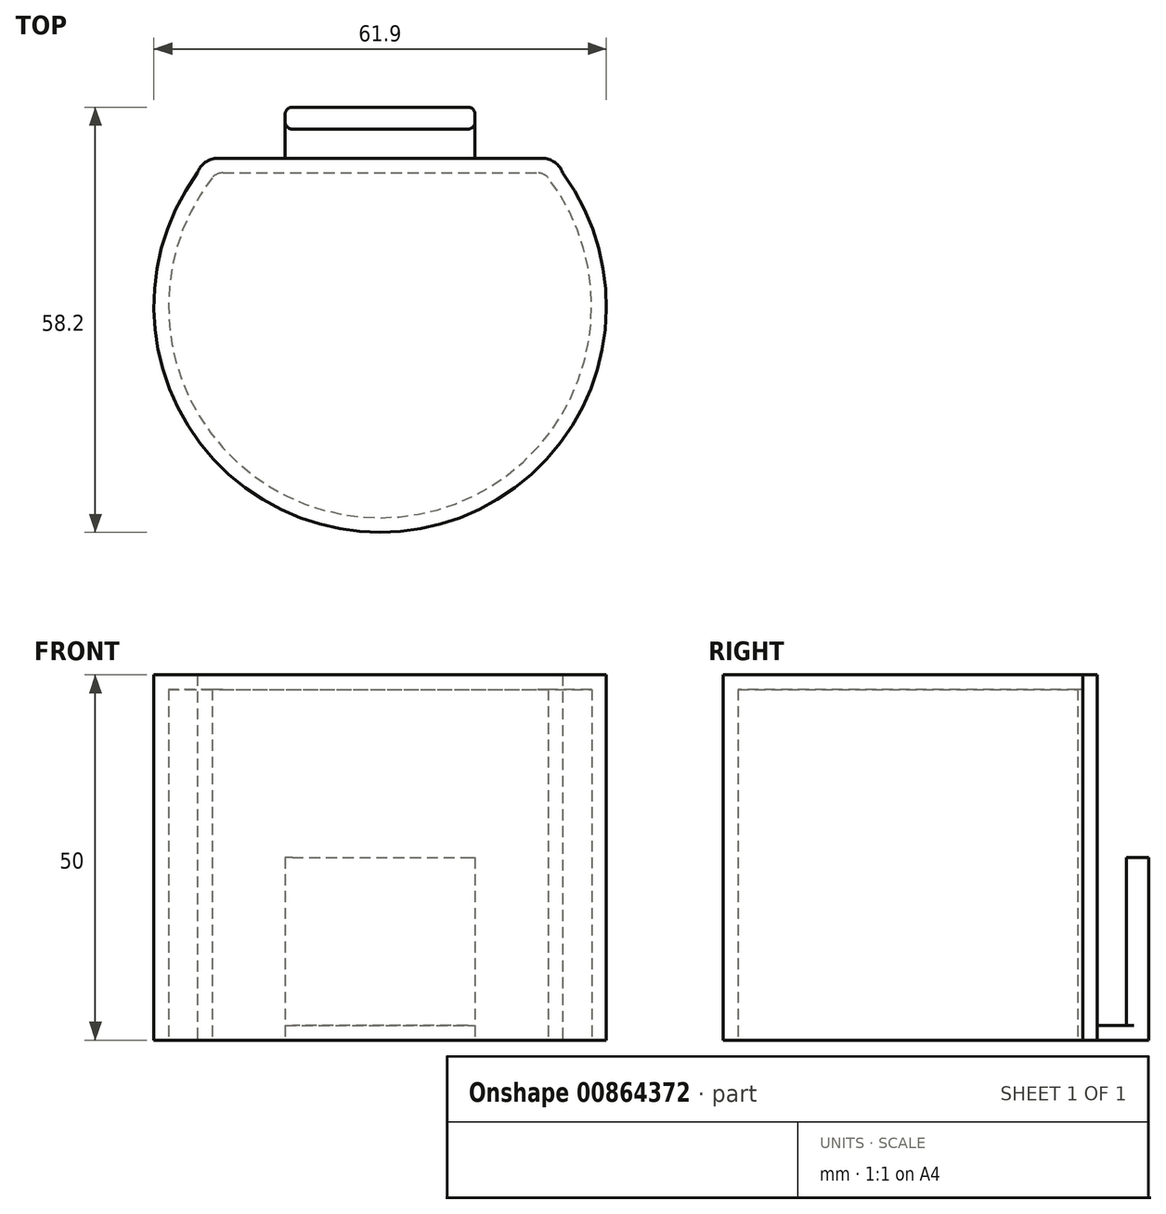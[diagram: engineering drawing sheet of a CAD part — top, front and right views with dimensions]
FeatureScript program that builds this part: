
annotation { "Feature Type Name" : "Feature", "Feature Type Description" : "" }
export const myFeature = defineFeature(function(context is Context, id is Id, definition is map)
    precondition{}
    {
        {
            var Q0;
            Q0=qCreatedBy(makeId("Top.planeOp"),FACE);
            var sketch = newSketch(context, id + "F0", { "sketchPlane" : qUnion([Q0])});
            skLineSegment(sketch, "E0", {"start": v(-13, 7) * mm, "end": v(13, 7) * mm});
            skLineSegment(sketch, "E1", {"start": v(13, 7) * mm, "end": v(13, 4) * mm});
            skLineSegment(sketch, "E2", {"start": v(13, 4) * mm, "end": v(-13, 4) * mm});
            skLineSegment(sketch, "E3", {"start": v(-13, 7) * mm, "end": v(-13, 4) * mm});
            skLineSegment(sketch, "E4.bottom", {"start": v(-13, 4) * mm, "end": v(13, 4) * mm});
            skLineSegment(sketch, "E4.top", {"start": v(-13, 0) * mm, "end": v(13, 0) * mm});
            skLineSegment(sketch, "E4.left", {"start": v(-13, 4) * mm, "end": v(-13, 0) * mm});
            skLineSegment(sketch, "E4.right", {"start": v(13, 4) * mm, "end": v(13, 0) * mm});
            skLineSegment(sketch, "E5.bottom", {"start": v(-25, 0) * mm, "end": v(25, 0) * mm});
            skLineSegment(sketch, "E5.top", {"start": v(-25, -2) * mm, "end": v(25, -2) * mm});
            skLineSegment(sketch, "E5.left", {"start": v(-25, 0) * mm, "end": v(-25, -2) * mm});
            skLineSegment(sketch, "E5.right", {"start": v(25, 0) * mm, "end": v(25, -2) * mm});
            skArc(sketch, "E6", {"start": v(-25, -2) * mm, "mid": v(0, -51.2) * mm, "end": v(25, -2) * mm});
            skSolve(sketch);
        }
        {
            var Q0;
            Q0=makeQuery(id+"F0.imprint","IMPRINT",FACE,{"disambiguationData":[TD([[makeQuery(id+"F0.imprint","IMPRINT",EDGE,{"derivedFrom":sQuery(id+"F0.wireOp",EDGE,"E0")}),-1.0]])]});
            extrude(context, id + "F1", {"entities" : qUnion([Q0]), "depth" : 25 * mm, "offsetDistance" : 25 * mm});
        }
        {
            var Q0;
            Q0=makeQuery(id+"F0.imprint","IMPRINT",FACE,{"disambiguationData":[TD([[makeQuery(id+"F0.imprint","IMPRINT",EDGE,{"derivedFrom":sQuery(id+"F0.wireOp",EDGE,"E2")}),1.0]])]});
            extrude(context, id + "F2", {"entities" : qUnion([Q0]), "operationType" : NewBodyOperationType.ADD, "depth" : 2 * mm, "offsetDistance" : 25 * mm});
        }
        {
            var Q0;
            {var subQ1=sQuery(id+"F0.wireOp",EDGE,"E4.top");Q0=makeQuery(id+"F0.imprint","IMPRINT",FACE,{"disambiguationData":[TD([[makeQuery(id+"F0.imprint","IMPRINT",EDGE,{"derivedFrom":subQ1}),-1.0]])]});}
            extrude(context, id + "F3", {"entities" : qUnion([Q0]), "operationType" : NewBodyOperationType.ADD, "depth" : 50 * mm, "offsetDistance" : 25 * mm});
        }
        {
            var Q0;
            Q0=makeQuery(id+"F0.imprint","IMPRINT",FACE,{"disambiguationData":[TD([[makeQuery(id+"F0.imprint","IMPRINT",EDGE,{"derivedFrom":sQuery(id+"F0.wireOp",EDGE,"E5.top")}),-1.0]])]});
            extrude(context, id + "F4", {"entities" : qUnion([Q0]), "operationType" : NewBodyOperationType.ADD, "depth" : 50 * mm, "offsetDistance" : 25 * mm});
        }
        {
            var Q0;
            {var subQ0=sQuery(id+"F0.wireOp",EDGE,"E5.top");var subQ1=sQuery(id+"F0.wireOp",EDGE,"E4.top");var subQ2=sQuery(id+"F0.wireOp",EDGE,"E2");Q0=makeQuery(id+"F4.boolean.opBoolean","MERGE",FACE,{"derivedFrom":[makeQuery(id+"F3.boolean.opBoolean","MERGE",FACE,{"derivedFrom":[makeQuery(id+"F2.boolean.opBoolean","MERGE",FACE,{"derivedFrom":[makeQuery(id+"F1.opExtrude","CAP_FACE",FACE,{"disambiguationData":[OSD([sQuery(id+"F0.wireOp",EDGE,"E0"),sQuery(id+"F0.wireOp",EDGE,"E1"),subQ2,sQuery(id+"F0.wireOp",EDGE,"E3")])],"isStart":true}),makeQuery(id+"F2.opExtrude","CAP_FACE",FACE,{"disambiguationData":[OSD([subQ2,subQ1,sQuery(id+"F0.wireOp",EDGE,"E4.left"),sQuery(id+"F0.wireOp",EDGE,"E4.right")])],"isStart":true})]}),makeQuery(id+"F3.opExtrude","CAP_FACE",FACE,{"disambiguationData":[OSD([subQ1,sQuery(id+"F0.wireOp",EDGE,"E5.bottom"),subQ0,sQuery(id+"F0.wireOp",EDGE,"E5.left"),sQuery(id+"F0.wireOp",EDGE,"E5.right")])],"isStart":true})]}),makeQuery(id+"F4.opExtrude","CAP_FACE",FACE,{"disambiguationData":[OSD([subQ0,sQuery(id+"F0.wireOp",EDGE,"E6")])],"isStart":true})]});}
            shell(context, id + "F5", {"entities" : qUnion([Q0]), "thickness" : 2 * mm});
        }
        {
            var Q0;
            Q0=makeQuery(id+"F3.opExtrude","SWEPT_EDGE",EDGE,{"disambiguationData":[OSD([sQuery(id+"F0.wireOp",EDGE,"E5.bottom"),sQuery(id+"F0.wireOp",EDGE,"E5.right")])]});
            fillet(context, id + "F6", {"entities" : qUnion([Q0]), "radius" : 3 * mm, "tangentPropagation" : true, "allowEdgeOverflow" : false});
        }
        {
            var Q0;
            Q0=makeQuery(id+"F3.opExtrude","SWEPT_EDGE",EDGE,{"disambiguationData":[OSD([sQuery(id+"F0.wireOp",EDGE,"E5.bottom"),sQuery(id+"F0.wireOp",EDGE,"E5.left")])]});
            fillet(context, id + "F7", {"entities" : qUnion([Q0]), "radius" : 3 * mm, "tangentPropagation" : true, "allowEdgeOverflow" : false});
        }
        {
            var Q0;
            Q0=makeQuery(id+"F1.opExtrude","SWEPT_EDGE",EDGE,{"disambiguationData":[OSD([sQuery(id+"F0.wireOp",EDGE,"E0"),sQuery(id+"F0.wireOp",EDGE,"E3")])]});
            fillet(context, id + "F8", {"entities" : qUnion([Q0]), "radius" : 1 * mm, "tangentPropagation" : true, "allowEdgeOverflow" : false});
        }
        {
            var Q0;
            Q0=makeQuery(id+"F1.opExtrude","SWEPT_EDGE",EDGE,{"disambiguationData":[OSD([sQuery(id+"F0.wireOp",EDGE,"E0"),sQuery(id+"F0.wireOp",EDGE,"E1")])]});
            fillet(context, id + "F9", {"entities" : qUnion([Q0]), "radius" : 1 * mm, "tangentPropagation" : true, "allowEdgeOverflow" : false});
        }
        {
            var Q0;
            Q0=makeQuery(id+"F1.opExtrude","SWEPT_EDGE",EDGE,{"disambiguationData":[OSD([sQuery(id+"F0.wireOp",EDGE,"E2"),sQuery(id+"F0.wireOp",EDGE,"E3"),sQuery(id+"F0.wireOp",EDGE,"E4.left")])]});
            fillet(context, id + "F10", {"entities" : qUnion([Q0]), "radius" : 1 * mm, "tangentPropagation" : true, "allowEdgeOverflow" : false});
        }
        {
            var Q0;
            Q0=makeQuery(id+"F1.opExtrude","SWEPT_EDGE",EDGE,{"disambiguationData":[OSD([sQuery(id+"F0.wireOp",EDGE,"E1"),sQuery(id+"F0.wireOp",EDGE,"E2"),sQuery(id+"F0.wireOp",EDGE,"E4.right")])]});
            fillet(context, id + "F11", {"entities" : qUnion([Q0]), "radius" : 1 * mm, "tangentPropagation" : true, "allowEdgeOverflow" : false});
        }
        {
            var Q0;
            Q0=makeQuery(id+"F5.opShell","OFFSET_EDGE",EDGE,{"disambiguationData":[OSD([sQuery(id+"F0.wireOp",EDGE,"E5.bottom"),sQuery(id+"F0.wireOp",EDGE,"E5.right")])]});
            fillet(context, id + "F12", {"entities" : qUnion([Q0]), "radius" : 2 * mm, "tangentPropagation" : true, "allowEdgeOverflow" : false});
        }
        {
            var Q0;
            Q0=makeQuery(id+"F5.opShell","OFFSET_EDGE",EDGE,{"disambiguationData":[OSD([sQuery(id+"F0.wireOp",EDGE,"E5.bottom"),sQuery(id+"F0.wireOp",EDGE,"E5.left")])]});
            fillet(context, id + "F13", {"entities" : qUnion([Q0]), "radius" : 2 * mm, "tangentPropagation" : true, "allowEdgeOverflow" : false});
        }
    });
